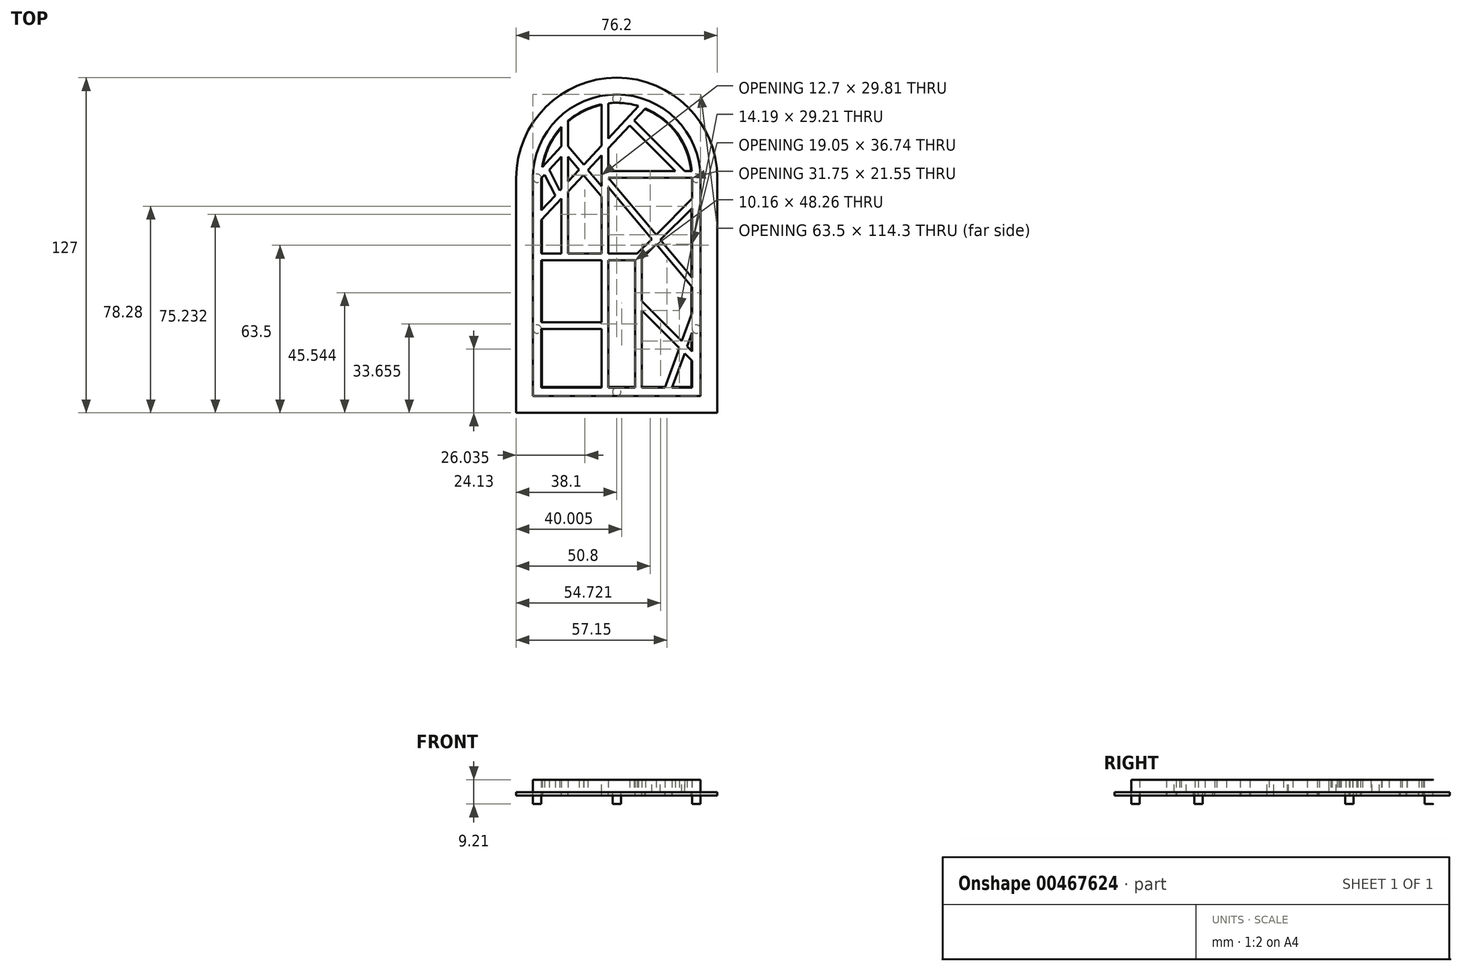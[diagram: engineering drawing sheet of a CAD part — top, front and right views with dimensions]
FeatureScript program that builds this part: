
annotation { "Feature Type Name" : "Feature", "Feature Type Description" : "" }
export const myFeature = defineFeature(function(context is Context, id is Id, definition is map)
    precondition{}
    {
        {
            var Q0;
            Q0=qCreatedBy(makeId("Top.planeOp"),FACE);
            var sketch = newSketch(context, id + "F0", { "sketchPlane" : qUnion([Q0])});
            skArc(sketch, "E0", {"start": v(31.75, 82.55) * mm, "mid": v(0, 114.3) * mm, "end": v(-31.75, 82.55) * mm});
            skLineSegment(sketch, "E1", {"start": v(31.75, 82.55) * mm, "end": v(31.75, 0) * mm});
            skLineSegment(sketch, "E2", {"start": v(31.75, 0) * mm, "end": v(-31.75, 0) * mm});
            skLineSegment(sketch, "E3", {"start": v(-31.75, 0) * mm, "end": v(-31.75, 82.55) * mm});
            skLineSegment(sketch, "E4.0", {"start": v(-28.58, 3.17) * mm, "end": v(-28.58, 82.55) * mm});
            skLineSegment(sketch, "E4.1", {"start": v(28.58, 3.18) * mm, "end": v(-28.58, 3.17) * mm});
            skLineSegment(sketch, "E4.2", {"start": v(28.57, 82.55) * mm, "end": v(28.58, 3.17) * mm});
            skArc(sketch, "E4.3", {"start": v(28.57, 82.55) * mm, "mid": v(0, 111.13) * mm, "end": v(-28.57, 82.55) * mm});
            skSolve(sketch);
        }
        {
            var Q0;
            Q0 = qSketchRegion(id + "F0", true);
            extrude(context, id + "F1", {"entities" : qUnion([Q0]), "depth" : 4.76 * mm});
        }
        {
            var Q0;
            Q0=qCreatedBy(makeId("Top.planeOp"),FACE);
            var sketch = newSketch(context, id + "F2", { "sketchPlane" : qUnion([Q0])});
            skLineSegment(sketch, "E5", {"start": v(-28.58, 53.98) * mm, "end": v(9.52, 53.98) * mm});
            skLineSegment(sketch, "E6", {"start": v(9.52, 53.98) * mm, "end": v(9.52, 3.17) * mm});
            skLineSegment(sketch, "E7", {"start": v(9.52, 3.17) * mm, "end": v(9.52, 3.17) * mm});
            skLineSegment(sketch, "E8", {"start": v(-28.58, 53.98) * mm, "end": v(-28.58, 51.43) * mm});
            skLineSegment(sketch, "E9", {"start": v(-28.58, 51.43) * mm, "end": v(6.98, 51.43) * mm});
            skLineSegment(sketch, "E10", {"start": v(6.98, 51.43) * mm, "end": v(6.98, 3.17) * mm});
            skLineSegment(sketch, "E11", {"start": v(6.98, 3.17) * mm, "end": v(9.52, 3.17) * mm});
            skSolve(sketch);
        }
        {
            var Q0;
            Q0 = qSketchRegion(id + "F2", true);
            var sketch = newSketch(context, id + "F3", { "sketchPlane" : qUnion([Q0])});
            skSolve(sketch);
        }
        {
            var Q0;
            Q0=makeQuery(id+"F3.imprint","IMPRINT",FACE,{"disambiguationData":[TD([[makeQuery(id+"F3.imprint","IMPRINT",EDGE,{"derivedFrom":makeQuery(id+"F2.imprint","IMPRINT",EDGE,{"derivedFrom":sQuery(id+"F2.wireOp",EDGE,"E5")})}),-1.0]])]});
            extrude(context, id + "F4", {"entities" : qUnion([Q0]), "operationType" : NewBodyOperationType.ADD, "depth" : 4.76 * mm});
        }
        {
            var Q0;
            Q0=qCreatedBy(makeId("Top.planeOp"),FACE);
            var sketch = newSketch(context, id + "F5", { "sketchPlane" : qUnion([Q0])});
            skLineSegment(sketch, "E12.bottom", {"start": v(-5.72, 3.17) * mm, "end": v(-3.18, 3.17) * mm});
            skLineSegment(sketch, "E12.left", {"start": v(-5.72, 3.17) * mm, "end": v(-5.72, 110.55) * mm});
            skLineSegment(sketch, "E12.right", {"start": v(-3.18, 3.17) * mm, "end": v(-3.18, 110.95) * mm});
            skArc(sketch, "E13.0", {"start": v(-3.18, 110.95) * mm, "mid": v(-4.45, 110.78) * mm, "end": v(-5.72, 110.55) * mm});
            skPoint(sketch, "E14.orphan", {"position": v(28.57, 82.55) * mm});
            skPoint(sketch, "E15.orphan", {"position": v(-28.57, 82.55) * mm});
            skSolve(sketch);
        }
        {
            var Q0;
            Q0 = qSketchRegion(id + "F5", true);
            extrude(context, id + "F6", {"entities" : qUnion([Q0]), "operationType" : NewBodyOperationType.ADD, "depth" : 4.76 * mm});
        }
        {
            var Q0;
            Q0=qCreatedBy(makeId("Top.planeOp"),FACE);
            var sketch = newSketch(context, id + "F7", { "sketchPlane" : qUnion([Q0])});
            skLineSegment(sketch, "E16.bottom", {"start": v(-28.58, 27.94) * mm, "end": v(-5.72, 27.94) * mm});
            skLineSegment(sketch, "E16.top", {"start": v(-28.58, 25.4) * mm, "end": v(-5.72, 25.4) * mm});
            skLineSegment(sketch, "E16.left", {"start": v(-28.58, 27.94) * mm, "end": v(-28.58, 25.4) * mm});
            skLineSegment(sketch, "E16.right", {"start": v(-5.72, 27.94) * mm, "end": v(-5.72, 25.4) * mm});
            skSolve(sketch);
        }
        {
            var Q0;
            Q0 = qSketchRegion(id + "F7", true);
            extrude(context, id + "F8", {"entities" : qUnion([Q0]), "operationType" : NewBodyOperationType.ADD, "depth" : 4.76 * mm});
        }
        {
            var Q0;
            Q0=qCreatedBy(makeId("Top.planeOp"),FACE);
            var sketch = newSketch(context, id + "F9", { "sketchPlane" : qUnion([Q0])});
            skLineSegment(sketch, "E17", {"start": v(9.52, 35.98) * mm, "end": v(28.58, 16.93) * mm});
            skLineSegment(sketch, "E18", {"start": v(28.58, 16.93) * mm, "end": v(28.58, 13.34) * mm});
            skLineSegment(sketch, "E19", {"start": v(28.58, 13.33) * mm, "end": v(9.52, 32.38) * mm});
            skLineSegment(sketch, "E20", {"start": v(9.52, 32.38) * mm, "end": v(9.52, 35.98) * mm});
            skLineSegment(sketch, "E21", {"start": v(-3.17, 82.7) * mm, "end": v(28.58, 44.87) * mm});
            skLineSegment(sketch, "E22", {"start": v(28.58, 44.87) * mm, "end": v(28.58, 41.28) * mm});
            skLineSegment(sketch, "E23", {"start": v(28.58, 41.27) * mm, "end": v(-3.18, 79.11) * mm});
            skLineSegment(sketch, "E24", {"start": v(-3.18, 79.11) * mm, "end": v(-3.18, 82.7) * mm});
            skSolve(sketch);
        }
        {
            var Q0;
            Q0 = qSketchRegion(id + "F9", true);
            extrude(context, id + "F10", {"entities" : qUnion([Q0]), "operationType" : NewBodyOperationType.ADD, "depth" : 4.76 * mm});
        }
        {
            var Q0;
            Q0=qCreatedBy(makeId("Top.planeOp"),FACE);
            var sketch = newSketch(context, id + "F11", { "sketchPlane" : qUnion([Q0])});
            skLineSegment(sketch, "E25.bottom", {"start": v(-20.96, 53.98) * mm, "end": v(-18.42, 53.98) * mm});
            skLineSegment(sketch, "E25.left", {"start": v(-20.96, 53.98) * mm, "end": v(-20.96, 101.98) * mm});
            skLineSegment(sketch, "E25.right", {"start": v(-18.42, 53.98) * mm, "end": v(-18.42, 104.4) * mm});
            skArc(sketch, "E26.0", {"start": v(-18.42, 104.4) * mm, "mid": v(-19.72, 103.23) * mm, "end": v(-20.96, 101.98) * mm});
            skPoint(sketch, "E27.orphan", {"position": v(-5.72, 110.55) * mm});
            skPoint(sketch, "E28.orphan", {"position": v(-28.57, 82.55) * mm});
            skSolve(sketch);
        }
        {
            var Q0;
            Q0 = qSketchRegion(id + "F11", true);
            extrude(context, id + "F12", {"entities" : qUnion([Q0]), "operationType" : NewBodyOperationType.ADD, "depth" : 4.76 * mm});
        }
        {
            var Q0;
            Q0=qCreatedBy(makeId("Top.planeOp"),FACE);
            var sketch = newSketch(context, id + "F13", { "sketchPlane" : qUnion([Q0])});
            skLineSegment(sketch, "E29", {"start": v(-28.58, 70.4) * mm, "end": v(8.26, 109.9) * mm});
            skLineSegment(sketch, "E30", {"start": v(10.87, 108.98) * mm, "end": v(-28.58, 66.67) * mm});
            skLineSegment(sketch, "E31", {"start": v(-28.58, 66.67) * mm, "end": v(-28.58, 70.4) * mm});
            skArc(sketch, "E32.0", {"start": v(10.87, 108.98) * mm, "mid": v(9.58, 109.47) * mm, "end": v(8.26, 109.9) * mm});
            skPoint(sketch, "E33.orphan", {"position": v(28.57, 82.55) * mm});
            skPoint(sketch, "E34.orphan", {"position": v(-3.18, 110.95) * mm});
            skLineSegment(sketch, "E35", {"start": v(7.73, 53.98) * mm, "end": v(9.52, 52.18) * mm});
            skLineSegment(sketch, "E36", {"start": v(9.52, 52.18) * mm, "end": v(28.58, 71.23) * mm});
            skLineSegment(sketch, "E37", {"start": v(28.58, 71.23) * mm, "end": v(28.58, 74.82) * mm});
            skLineSegment(sketch, "E38", {"start": v(28.58, 74.82) * mm, "end": v(7.73, 53.98) * mm});
            skLineSegment(sketch, "E39", {"start": v(18.25, 3.17) * mm, "end": v(28.58, 31.54) * mm});
            skLineSegment(sketch, "E40", {"start": v(28.58, 31.54) * mm, "end": v(28.58, 24.11) * mm});
            skLineSegment(sketch, "E41", {"start": v(28.58, 24.11) * mm, "end": v(20.96, 3.17) * mm});
            skLineSegment(sketch, "E42", {"start": v(20.96, 3.17) * mm, "end": v(18.25, 3.17) * mm});
            skSolve(sketch);
        }
        {
            var Q0;
            Q0 = qSketchRegion(id + "F13", true);
            extrude(context, id + "F14", {"entities" : qUnion([Q0]), "operationType" : NewBodyOperationType.ADD, "depth" : 4.76 * mm});
        }
        {
            var Q0;
            Q0=qCreatedBy(makeId("Top.planeOp"),FACE);
            var sketch = newSketch(context, id + "F15", { "sketchPlane" : qUnion([Q0])});
            skLineSegment(sketch, "E43", {"start": v(-18.42, 94.65) * mm, "end": v(-12.52, 87.62) * mm});
            skLineSegment(sketch, "E44", {"start": v(-5.72, 79.52) * mm, "end": v(-5.72, 75.57) * mm});
            skLineSegment(sketch, "E45", {"start": v(-5.72, 75.57) * mm, "end": v(-12.62, 83.79) * mm});
            skLineSegment(sketch, "E46", {"start": v(-18.42, 90.7) * mm, "end": v(-18.42, 94.65) * mm});
            skLineSegment(sketch, "E47", {"start": v(-20.96, 94.65) * mm, "end": v(-28.25, 86.83) * mm});
            skLineSegment(sketch, "E48", {"start": v(-28.58, 82.55) * mm, "end": v(-20.96, 90.72) * mm});
            skLineSegment(sketch, "E49", {"start": v(-20.96, 94.65) * mm, "end": v(-20.96, 90.72) * mm});
            skLineSegment(sketch, "E50.bottom", {"start": v(-3.18, 85.25) * mm, "end": v(28.45, 85.25) * mm});
            skLineSegment(sketch, "E50.top", {"start": v(-3.17, 82.7) * mm, "end": v(28.57, 82.7) * mm});
            skLineSegment(sketch, "E50.left", {"start": v(-3.18, 85.25) * mm, "end": v(-3.18, 82.7) * mm});
            skPoint(sketch, "E51.orphan", {"position": v(10.87, 108.98) * mm});
            skPoint(sketch, "E52.orphan", {"position": v(28.57, 82.55) * mm});
            skLineSegment(sketch, "E53.0", {"start": v(-10.87, 85.66) * mm, "end": v(-12.62, 83.79) * mm});
            skLineSegment(sketch, "E53.1", {"start": v(-14.26, 85.75) * mm, "end": v(-12.52, 87.62) * mm});
            skLineSegment(sketch, "E54.trimOffspring", {"start": v(-10.87, 85.66) * mm, "end": v(-5.72, 79.52) * mm});
            skLineSegment(sketch, "E55.trimOffspring", {"start": v(-14.26, 85.75) * mm, "end": v(-18.42, 90.7) * mm});
            skArc(sketch, "E56.0", {"start": v(-28.25, 86.83) * mm, "mid": v(-28.5, 84.7) * mm, "end": v(-28.58, 82.55) * mm});
            skPoint(sketch, "E57.orphan", {"position": v(-28.57, 82.55) * mm});
            skArc(sketch, "E58.0", {"start": v(28.57, 82.7) * mm, "mid": v(28.54, 83.98) * mm, "end": v(28.45, 85.25) * mm});
            skSolve(sketch);
        }
        {
            var Q0;
            Q0 = qSketchRegion(id + "F15", true);
            extrude(context, id + "F16", {"entities" : qUnion([Q0]), "operationType" : NewBodyOperationType.ADD, "depth" : 4.76 * mm});
        }
        {
            var Q0;
            Q0=qCreatedBy(makeId("Top.planeOp"),FACE);
            var sketch = newSketch(context, id + "F17", { "sketchPlane" : qUnion([Q0])});
            skLineSegment(sketch, "E59", {"start": v(4.9, 102.57) * mm, "end": v(22.23, 85.25) * mm});
            skLineSegment(sketch, "E60", {"start": v(22.22, 85.25) * mm, "end": v(25.82, 85.25) * mm});
            skLineSegment(sketch, "E61", {"start": v(25.82, 85.25) * mm, "end": v(6.63, 104.43) * mm});
            skLineSegment(sketch, "E62", {"start": v(6.63, 104.43) * mm, "end": v(4.9, 102.57) * mm});
            skLineSegment(sketch, "E63", {"start": v(-27.33, 83.89) * mm, "end": v(-23.32, 76.03) * mm});
            skLineSegment(sketch, "E64", {"start": v(-23.32, 76.03) * mm, "end": v(-21.6, 77.89) * mm});
            skLineSegment(sketch, "E65", {"start": v(-21.6, 77.89) * mm, "end": v(-25.6, 85.75) * mm});
            skLineSegment(sketch, "E66", {"start": v(-25.6, 85.75) * mm, "end": v(-27.33, 83.89) * mm});
            skSolve(sketch);
        }
        {
            var Q0;
            Q0 = qSketchRegion(id + "F17", true);
            extrude(context, id + "F18", {"entities" : qUnion([Q0]), "operationType" : NewBodyOperationType.ADD, "depth" : 4.76 * mm});
        }
        {
            var Q0;
            Q0=makeQuery(id+"F18.boolean.opBoolean","MERGE",FACE,{"derivedFrom":[makeQuery(id+"F16.boolean.opBoolean","MERGE",FACE,{"derivedFrom":[makeQuery(id+"F14.boolean.opBoolean","MERGE",FACE,{"derivedFrom":[makeQuery(id+"F12.boolean.opBoolean","MERGE",FACE,{"derivedFrom":[makeQuery(id+"F10.boolean.opBoolean","MERGE",FACE,{"derivedFrom":[makeQuery(id+"F8.boolean.opBoolean","MERGE",FACE,{"derivedFrom":[makeQuery(id+"F6.boolean.opBoolean","MERGE",FACE,{"derivedFrom":[makeQuery(id+"F4.boolean.opBoolean","MERGE",FACE,{"derivedFrom":[makeQuery(id+"F1.opExtrude","CAP_FACE",FACE,{"disambiguationData":[OSD([sQuery(id+"F0.wireOp",EDGE,"E0"),sQuery(id+"F0.wireOp",EDGE,"E1"),sQuery(id+"F0.wireOp",EDGE,"E2"),sQuery(id+"F0.wireOp",EDGE,"E3"),sQuery(id+"F0.wireOp",EDGE,"E4.0"),sQuery(id+"F0.wireOp",EDGE,"E4.1"),sQuery(id+"F0.wireOp",EDGE,"E4.2"),sQuery(id+"F0.wireOp",EDGE,"E4.3")])],"isStart":true}),makeQuery(id+"F4.opExtrude","CAP_FACE",FACE,{"disambiguationData":[OSD([sQuery(id+"F2.wireOp",EDGE,"E5"),sQuery(id+"F2.wireOp",EDGE,"E6"),sQuery(id+"F2.wireOp",EDGE,"E8"),sQuery(id+"F2.wireOp",EDGE,"E9"),sQuery(id+"F2.wireOp",EDGE,"E10"),sQuery(id+"F2.wireOp",EDGE,"E11")])],"isStart":true})]}),makeQuery(id+"F6.opExtrude","CAP_FACE",FACE,{"disambiguationData":[OSD([sQuery(id+"F5.wireOp",EDGE,"E12.bottom"),sQuery(id+"F5.wireOp",EDGE,"E12.left"),sQuery(id+"F5.wireOp",EDGE,"E12.right"),sQuery(id+"F5.wireOp",EDGE,"E13.0")])],"isStart":true})]}),makeQuery(id+"F8.opExtrude","CAP_FACE",FACE,{"disambiguationData":[OSD([sQuery(id+"F7.wireOp",EDGE,"E16.bottom"),sQuery(id+"F7.wireOp",EDGE,"E16.top"),sQuery(id+"F7.wireOp",EDGE,"E16.left"),sQuery(id+"F7.wireOp",EDGE,"E16.right")])],"isStart":true})]}),makeQuery(id+"F10.opExtrude","CAP_FACE",FACE,{"disambiguationData":[OSD([sQuery(id+"F9.wireOp",EDGE,"E17"),sQuery(id+"F9.wireOp",EDGE,"E18"),sQuery(id+"F9.wireOp",EDGE,"E19"),sQuery(id+"F9.wireOp",EDGE,"E20")])],"isStart":true}),makeQuery(id+"F10.opExtrude","CAP_FACE",FACE,{"disambiguationData":[OSD([sQuery(id+"F9.wireOp",EDGE,"E21"),sQuery(id+"F9.wireOp",EDGE,"E22"),sQuery(id+"F9.wireOp",EDGE,"E23"),sQuery(id+"F9.wireOp",EDGE,"E24")])],"isStart":true})]}),makeQuery(id+"F12.opExtrude","CAP_FACE",FACE,{"disambiguationData":[OSD([sQuery(id+"F11.wireOp",EDGE,"E25.bottom"),sQuery(id+"F11.wireOp",EDGE,"E25.left"),sQuery(id+"F11.wireOp",EDGE,"E25.right"),sQuery(id+"F11.wireOp",EDGE,"E26.0")])],"isStart":true})]}),makeQuery(id+"F14.opExtrude","CAP_FACE",FACE,{"disambiguationData":[OSD([sQuery(id+"F13.wireOp",EDGE,"E29"),sQuery(id+"F13.wireOp",EDGE,"E30"),sQuery(id+"F13.wireOp",EDGE,"E31"),sQuery(id+"F13.wireOp",EDGE,"E32.0")])],"isStart":true}),makeQuery(id+"F14.opExtrude","CAP_FACE",FACE,{"disambiguationData":[OSD([sQuery(id+"F13.wireOp",EDGE,"E35"),sQuery(id+"F13.wireOp",EDGE,"E36"),sQuery(id+"F13.wireOp",EDGE,"E37"),sQuery(id+"F13.wireOp",EDGE,"E38")])],"isStart":true}),makeQuery(id+"F14.opExtrude","CAP_FACE",FACE,{"disambiguationData":[OSD([sQuery(id+"F13.wireOp",EDGE,"E39"),sQuery(id+"F13.wireOp",EDGE,"E40"),sQuery(id+"F13.wireOp",EDGE,"E41"),sQuery(id+"F13.wireOp",EDGE,"E42")])],"isStart":true})]}),makeQuery(id+"F16.opExtrude","CAP_FACE",FACE,{"disambiguationData":[OSD([sQuery(id+"F15.wireOp",EDGE,"E43"),sQuery(id+"F15.wireOp",EDGE,"E46"),sQuery(id+"F15.wireOp",EDGE,"E53.1"),sQuery(id+"F15.wireOp",EDGE,"E55.trimOffspring")])],"isStart":true}),makeQuery(id+"F16.opExtrude","CAP_FACE",FACE,{"disambiguationData":[OSD([sQuery(id+"F15.wireOp",EDGE,"E44"),sQuery(id+"F15.wireOp",EDGE,"E45"),sQuery(id+"F15.wireOp",EDGE,"E53.0"),sQuery(id+"F15.wireOp",EDGE,"E54.trimOffspring")])],"isStart":true}),makeQuery(id+"F16.opExtrude","CAP_FACE",FACE,{"disambiguationData":[OSD([sQuery(id+"F15.wireOp",EDGE,"E47"),sQuery(id+"F15.wireOp",EDGE,"E48"),sQuery(id+"F15.wireOp",EDGE,"E49"),sQuery(id+"F15.wireOp",EDGE,"E56.0")])],"isStart":true}),makeQuery(id+"F16.opExtrude","CAP_FACE",FACE,{"disambiguationData":[OSD([sQuery(id+"F15.wireOp",EDGE,"E50.bottom"),sQuery(id+"F15.wireOp",EDGE,"E50.top"),sQuery(id+"F15.wireOp",EDGE,"E50.left"),sQuery(id+"F15.wireOp",EDGE,"E58.0")])],"isStart":true})]}),makeQuery(id+"F18.opExtrude","CAP_FACE",FACE,{"disambiguationData":[OSD([sQuery(id+"F17.wireOp",EDGE,"E59"),sQuery(id+"F17.wireOp",EDGE,"E60"),sQuery(id+"F17.wireOp",EDGE,"E61"),sQuery(id+"F17.wireOp",EDGE,"E62")])],"isStart":true}),makeQuery(id+"F18.opExtrude","CAP_FACE",FACE,{"disambiguationData":[OSD([sQuery(id+"F17.wireOp",EDGE,"E63"),sQuery(id+"F17.wireOp",EDGE,"E64"),sQuery(id+"F17.wireOp",EDGE,"E65"),sQuery(id+"F17.wireOp",EDGE,"E66")])],"isStart":true})]});
            var sketch = newSketch(context, id + "F19", { "sketchPlane" : qUnion([Q0])});
            skCircle(sketch, "E67", {"center": v(0, -112.71) * mm, "radius": 1.59 * mm});
            skLineSegment(sketch, "E68", {"start": v(0, -114.3) * mm, "end": v(0, -111.13) * mm, "construction": true});
            skLineSegment(sketch, "E69", {"start": v(28.57, -82.55) * mm, "end": v(31.75, -82.55) * mm, "construction": true});
            skLineSegment(sketch, "E70", {"start": v(-28.58, -82.55) * mm, "end": v(-31.75, -82.55) * mm, "construction": true});
            skLineSegment(sketch, "E71", {"start": v(0, 0) * mm, "end": v(0, -3.17) * mm, "construction": true});
            skLineSegment(sketch, "E72", {"start": v(31.75, -25.4) * mm, "end": v(28.58, -25.4) * mm, "construction": true});
            skLineSegment(sketch, "E73", {"start": v(-31.75, -25.4) * mm, "end": v(-28.58, -25.4) * mm, "construction": true});
            skLineSegment(sketch, "E74", {"start": v(28.58, -25.4) * mm, "end": v(-28.58, -25.4) * mm, "construction": true});
            skCircle(sketch, "E75", {"center": v(-30.16, -25.4) * mm, "radius": 1.59 * mm});
            skCircle(sketch, "E76", {"center": v(30.16, -25.4) * mm, "radius": 1.59 * mm});
            skCircle(sketch, "E77", {"center": v(0, -1.59) * mm, "radius": 1.59 * mm});
            skCircle(sketch, "E78", {"center": v(-30.16, -82.55) * mm, "radius": 1.59 * mm});
            skCircle(sketch, "E79", {"center": v(30.16, -82.55) * mm, "radius": 1.59 * mm});
            skSolve(sketch);
        }
        {
            var Q0;
            Q0 = qSketchRegion(id + "F19", true);
            extrude(context, id + "F20", {"entities" : qUnion([Q0]), "operationType" : NewBodyOperationType.ADD, "depth" : 4.44 * mm});
        }
        {
            var Q0;
            Q0=makeQuery(id+"F18.boolean.opBoolean","MERGE",FACE,{"derivedFrom":[makeQuery(id+"F16.boolean.opBoolean","MERGE",FACE,{"derivedFrom":[makeQuery(id+"F14.boolean.opBoolean","MERGE",FACE,{"derivedFrom":[makeQuery(id+"F12.boolean.opBoolean","MERGE",FACE,{"derivedFrom":[makeQuery(id+"F10.boolean.opBoolean","MERGE",FACE,{"derivedFrom":[makeQuery(id+"F8.boolean.opBoolean","MERGE",FACE,{"derivedFrom":[makeQuery(id+"F6.boolean.opBoolean","MERGE",FACE,{"derivedFrom":[makeQuery(id+"F4.boolean.opBoolean","MERGE",FACE,{"derivedFrom":[makeQuery(id+"F1.opExtrude","CAP_FACE",FACE,{"disambiguationData":[OSD([sQuery(id+"F0.wireOp",EDGE,"E0"),sQuery(id+"F0.wireOp",EDGE,"E1"),sQuery(id+"F0.wireOp",EDGE,"E2"),sQuery(id+"F0.wireOp",EDGE,"E3"),sQuery(id+"F0.wireOp",EDGE,"E4.0"),sQuery(id+"F0.wireOp",EDGE,"E4.1"),sQuery(id+"F0.wireOp",EDGE,"E4.2"),sQuery(id+"F0.wireOp",EDGE,"E4.3")])],"isStart":true}),makeQuery(id+"F4.opExtrude","CAP_FACE",FACE,{"disambiguationData":[OSD([sQuery(id+"F2.wireOp",EDGE,"E5"),sQuery(id+"F2.wireOp",EDGE,"E6"),sQuery(id+"F2.wireOp",EDGE,"E8"),sQuery(id+"F2.wireOp",EDGE,"E9"),sQuery(id+"F2.wireOp",EDGE,"E10"),sQuery(id+"F2.wireOp",EDGE,"E11")])],"isStart":true})]}),makeQuery(id+"F6.opExtrude","CAP_FACE",FACE,{"disambiguationData":[OSD([sQuery(id+"F5.wireOp",EDGE,"E12.bottom"),sQuery(id+"F5.wireOp",EDGE,"E12.left"),sQuery(id+"F5.wireOp",EDGE,"E12.right"),sQuery(id+"F5.wireOp",EDGE,"E13.0")])],"isStart":true})]}),makeQuery(id+"F8.opExtrude","CAP_FACE",FACE,{"disambiguationData":[OSD([sQuery(id+"F7.wireOp",EDGE,"E16.bottom"),sQuery(id+"F7.wireOp",EDGE,"E16.top"),sQuery(id+"F7.wireOp",EDGE,"E16.left"),sQuery(id+"F7.wireOp",EDGE,"E16.right")])],"isStart":true})]}),makeQuery(id+"F10.opExtrude","CAP_FACE",FACE,{"disambiguationData":[OSD([sQuery(id+"F9.wireOp",EDGE,"E17"),sQuery(id+"F9.wireOp",EDGE,"E18"),sQuery(id+"F9.wireOp",EDGE,"E19"),sQuery(id+"F9.wireOp",EDGE,"E20")])],"isStart":true}),makeQuery(id+"F10.opExtrude","CAP_FACE",FACE,{"disambiguationData":[OSD([sQuery(id+"F9.wireOp",EDGE,"E21"),sQuery(id+"F9.wireOp",EDGE,"E22"),sQuery(id+"F9.wireOp",EDGE,"E23"),sQuery(id+"F9.wireOp",EDGE,"E24")])],"isStart":true})]}),makeQuery(id+"F12.opExtrude","CAP_FACE",FACE,{"disambiguationData":[OSD([sQuery(id+"F11.wireOp",EDGE,"E25.bottom"),sQuery(id+"F11.wireOp",EDGE,"E25.left"),sQuery(id+"F11.wireOp",EDGE,"E25.right"),sQuery(id+"F11.wireOp",EDGE,"E26.0")])],"isStart":true})]}),makeQuery(id+"F14.opExtrude","CAP_FACE",FACE,{"disambiguationData":[OSD([sQuery(id+"F13.wireOp",EDGE,"E29"),sQuery(id+"F13.wireOp",EDGE,"E30"),sQuery(id+"F13.wireOp",EDGE,"E31"),sQuery(id+"F13.wireOp",EDGE,"E32.0")])],"isStart":true}),makeQuery(id+"F14.opExtrude","CAP_FACE",FACE,{"disambiguationData":[OSD([sQuery(id+"F13.wireOp",EDGE,"E35"),sQuery(id+"F13.wireOp",EDGE,"E36"),sQuery(id+"F13.wireOp",EDGE,"E37"),sQuery(id+"F13.wireOp",EDGE,"E38")])],"isStart":true}),makeQuery(id+"F14.opExtrude","CAP_FACE",FACE,{"disambiguationData":[OSD([sQuery(id+"F13.wireOp",EDGE,"E39"),sQuery(id+"F13.wireOp",EDGE,"E40"),sQuery(id+"F13.wireOp",EDGE,"E41"),sQuery(id+"F13.wireOp",EDGE,"E42")])],"isStart":true})]}),makeQuery(id+"F16.opExtrude","CAP_FACE",FACE,{"disambiguationData":[OSD([sQuery(id+"F15.wireOp",EDGE,"E43"),sQuery(id+"F15.wireOp",EDGE,"E46"),sQuery(id+"F15.wireOp",EDGE,"E53.1"),sQuery(id+"F15.wireOp",EDGE,"E55.trimOffspring")])],"isStart":true}),makeQuery(id+"F16.opExtrude","CAP_FACE",FACE,{"disambiguationData":[OSD([sQuery(id+"F15.wireOp",EDGE,"E44"),sQuery(id+"F15.wireOp",EDGE,"E45"),sQuery(id+"F15.wireOp",EDGE,"E53.0"),sQuery(id+"F15.wireOp",EDGE,"E54.trimOffspring")])],"isStart":true}),makeQuery(id+"F16.opExtrude","CAP_FACE",FACE,{"disambiguationData":[OSD([sQuery(id+"F15.wireOp",EDGE,"E47"),sQuery(id+"F15.wireOp",EDGE,"E48"),sQuery(id+"F15.wireOp",EDGE,"E49"),sQuery(id+"F15.wireOp",EDGE,"E56.0")])],"isStart":true}),makeQuery(id+"F16.opExtrude","CAP_FACE",FACE,{"disambiguationData":[OSD([sQuery(id+"F15.wireOp",EDGE,"E50.bottom"),sQuery(id+"F15.wireOp",EDGE,"E50.top"),sQuery(id+"F15.wireOp",EDGE,"E50.left"),sQuery(id+"F15.wireOp",EDGE,"E58.0")])],"isStart":true})]}),makeQuery(id+"F18.opExtrude","CAP_FACE",FACE,{"disambiguationData":[OSD([sQuery(id+"F17.wireOp",EDGE,"E59"),sQuery(id+"F17.wireOp",EDGE,"E60"),sQuery(id+"F17.wireOp",EDGE,"E61"),sQuery(id+"F17.wireOp",EDGE,"E62")])],"isStart":true}),makeQuery(id+"F18.opExtrude","CAP_FACE",FACE,{"disambiguationData":[OSD([sQuery(id+"F17.wireOp",EDGE,"E63"),sQuery(id+"F17.wireOp",EDGE,"E64"),sQuery(id+"F17.wireOp",EDGE,"E65"),sQuery(id+"F17.wireOp",EDGE,"E66")])],"isStart":true})]});
            var sketch = newSketch(context, id + "F21", { "sketchPlane" : qUnion([Q0])});
            skLineSegment(sketch, "E80.0", {"start": v(-31.75, -25.4) * mm, "end": v(-31.75, -82.55) * mm, "construction": true});
            skArc(sketch, "E80.1", {"start": v(0, -114.3) * mm, "mid": v(-22.45, -105) * mm, "end": v(-31.75, -82.55) * mm, "construction": true});
            skArc(sketch, "E80.2", {"start": v(31.75, -82.55) * mm, "mid": v(22.45, -105) * mm, "end": v(0, -114.3) * mm, "construction": true});
            skLineSegment(sketch, "E80.3", {"start": v(31.75, -82.55) * mm, "end": v(31.75, -25.4) * mm, "construction": true});
            skLineSegment(sketch, "E80.4", {"start": v(31.75, -25.4) * mm, "end": v(31.75, 0) * mm, "construction": true});
            skLineSegment(sketch, "E80.5", {"start": v(31.75, 0) * mm, "end": v(0, 0) * mm, "construction": true});
            skLineSegment(sketch, "E80.6", {"start": v(0, 0) * mm, "end": v(-31.75, 0) * mm, "construction": true});
            skLineSegment(sketch, "E80.7", {"start": v(-31.75, 0) * mm, "end": v(-31.75, -25.4) * mm, "construction": true});
            skLineSegment(sketch, "E81.0", {"start": v(28.32, -82.55) * mm, "end": v(28.32, -25.4) * mm});
            skLineSegment(sketch, "E81.1", {"start": v(28.32, -25.4) * mm, "end": v(28.32, -3.43) * mm});
            skArc(sketch, "E81.2", {"start": v(28.32, -82.55) * mm, "mid": v(20.03, -102.58) * mm, "end": v(0, -110.87) * mm});
            skLineSegment(sketch, "E81.3", {"start": v(28.32, -3.43) * mm, "end": v(0, -3.43) * mm});
            skArc(sketch, "E81.4", {"start": v(0, -110.87) * mm, "mid": v(-20.03, -102.58) * mm, "end": v(-28.32, -82.55) * mm});
            skLineSegment(sketch, "E81.5", {"start": v(-28.32, -25.4) * mm, "end": v(-28.32, -82.55) * mm});
            skLineSegment(sketch, "E81.6", {"start": v(-28.32, -3.43) * mm, "end": v(-28.32, -25.4) * mm});
            skLineSegment(sketch, "E81.7", {"start": v(0, -3.43) * mm, "end": v(-28.32, -3.43) * mm});
            skLineSegment(sketch, "E82.0", {"start": v(-38.1, 6.35) * mm, "end": v(-38.1, -25.4) * mm});
            skLineSegment(sketch, "E82.1", {"start": v(0, 6.35) * mm, "end": v(-38.1, 6.35) * mm});
            skLineSegment(sketch, "E82.2", {"start": v(-38.1, -25.4) * mm, "end": v(-38.1, -82.55) * mm});
            skLineSegment(sketch, "E82.3", {"start": v(38.1, 6.35) * mm, "end": v(0, 6.35) * mm});
            skArc(sketch, "E82.4", {"start": v(0, -120.65) * mm, "mid": v(-26.94, -109.5) * mm, "end": v(-38.1, -82.55) * mm});
            skArc(sketch, "E82.5", {"start": v(38.1, -82.55) * mm, "mid": v(26.94, -109.5) * mm, "end": v(0, -120.65) * mm});
            skLineSegment(sketch, "E82.6", {"start": v(38.1, -82.55) * mm, "end": v(38.1, -25.4) * mm});
            skLineSegment(sketch, "E82.7", {"start": v(38.1, -25.4) * mm, "end": v(38.1, 6.35) * mm});
            skSolve(sketch);
        }
        {
            var Q0;
            {var subQ28=sQuery(id+"F19.wireOp",EDGE,"E67");Q0=makeQuery(id+"F21.imprint","IMPRINT",FACE,{"disambiguationData":[TD([[makeQuery(id+"F21.imprint","IMPRINT",EDGE,{"derivedFrom":makeQuery(id+"F20.boolean.opBoolean","SPLIT",EDGE,{"disambiguationData":[OD(0.0)],"derivedFrom":makeQuery(id+"F20.opExtrude","CAP_EDGE",EDGE,{"disambiguationData":[OSD([subQ28])],"isStart":true})})}),-1.0]])]});}
            var Q1;
            {var subQ39=sQuery(id+"F19.wireOp",EDGE,"E76");Q1=makeQuery(id+"F21.imprint","IMPRINT",FACE,{"disambiguationData":[TD([[makeQuery(id+"F21.imprint","IMPRINT",EDGE,{"derivedFrom":makeQuery(id+"F20.opExtrude","CAP_EDGE",EDGE,{"disambiguationData":[OSD([subQ39])],"isStart":true})}),-1.0]])]});}
            var Q2;
            {var subQ21=sQuery(id+"F21.wireOp",EDGE,"E81.2");var subQ26=sQuery(id+"F21.wireOp",EDGE,"E81.0");var subQ27=makeQuery(id+"F21.imprint","INTERSECT",VERTEX,{"derivedFrom":[subQ26,subQ21]});Q2=makeQuery(id+"F21.imprint","IMPRINT",FACE,{"disambiguationData":[TD([[makeQuery(id+"F21.imprint","IMPRINT",EDGE,{"disambiguationData":[TD([[subQ27,-1.0]])],"derivedFrom":subQ21}),1.0]])]});}
            var Q3;
            Q3=makeQuery(id+"F21.imprint","IMPRINT",FACE,{"disambiguationData":[TD([[makeQuery(id+"F21.imprint","IMPRINT",EDGE,{"derivedFrom":sQuery(id+"F21.wireOp",EDGE,"E82.0")}),1.0]])]});
            var Q4;
            {var subQ1=sQuery(id+"F13.wireOp",EDGE,"E30");var subQ8=sQuery(id+"F0.wireOp",EDGE,"E4.3");var subQ9=sQuery(id+"F0.wireOp",EDGE,"E4.2");var subQ28=makeQuery(id+"F14.opExtrude","SWEPT_FACE",FACE,{"disambiguationData":[OSD([subQ1])]});var subQ32=makeQuery(id+"F1.opExtrude","SWEPT_FACE",FACE,{"disambiguationData":[OSD([subQ9])]});var subQ33=makeQuery(id+"F16.boolean.opBoolean","SPLIT",EDGE,{"disambiguationData":[TD([subQ28])],"derivedFrom":makeQuery(id+"F14.boolean.opBoolean","SPLIT",EDGE,{"disambiguationData":[TD([subQ32])],"derivedFrom":makeQuery(id+"F6.boolean.opBoolean","SPLIT",EDGE,{"disambiguationData":[TD([subQ32])],"derivedFrom":makeQuery(id+"F1.opExtrude","CAP_EDGE",EDGE,{"disambiguationData":[OSD([subQ8])],"isStart":true})})})});Q4=makeQuery(id+"F21.imprint","IMPRINT",FACE,{"disambiguationData":[TD([[makeQuery(id+"F21.imprint","IMPRINT",EDGE,{"derivedFrom":subQ33}),-1.0]])]});}
            var Q5;
            {var subQ28=sQuery(id+"F21.wireOp",EDGE,"E81.4");var subQ29=sQuery(id+"F21.wireOp",EDGE,"E81.2");var subQ30=makeQuery(id+"F21.imprint","INTERSECT",VERTEX,{"derivedFrom":[subQ29,subQ28]});Q5=makeQuery(id+"F21.imprint","IMPRINT",FACE,{"disambiguationData":[TD([[makeQuery(id+"F21.imprint","IMPRINT",EDGE,{"disambiguationData":[TD([[subQ30,1.0]])],"derivedFrom":subQ29}),1.0]])]});}
            var Q6;
            {var subQ3=sQuery(id+"F19.wireOp",EDGE,"E67");Q6=makeQuery(id+"F21.imprint","IMPRINT",FACE,{"disambiguationData":[TD([[makeQuery(id+"F21.imprint","IMPRINT",EDGE,{"derivedFrom":makeQuery(id+"F20.boolean.opBoolean","SPLIT",EDGE,{"disambiguationData":[OD(1.0)],"derivedFrom":makeQuery(id+"F20.opExtrude","CAP_EDGE",EDGE,{"disambiguationData":[OSD([subQ3])],"isStart":true})})}),-1.0]])]});}
            var Q7;
            {var subQ4=sQuery(id+"F5.wireOp",EDGE,"E12.left");var subQ5=makeQuery(id+"F6.opExtrude","SWEPT_FACE",FACE,{"disambiguationData":[OSD([subQ4])]});var subQ8=sQuery(id+"F0.wireOp",EDGE,"E4.3");var subQ9=sQuery(id+"F0.wireOp",EDGE,"E4.0");var subQ26=makeQuery(id+"F12.boolean.opBoolean","SPLIT",EDGE,{"disambiguationData":[TD([subQ5])],"derivedFrom":makeQuery(id+"F6.boolean.opBoolean","SPLIT",EDGE,{"disambiguationData":[TD([makeQuery(id+"F1.opExtrude","SWEPT_FACE",FACE,{"disambiguationData":[OSD([subQ9])]})])],"derivedFrom":makeQuery(id+"F1.opExtrude","CAP_EDGE",EDGE,{"disambiguationData":[OSD([subQ8])],"isStart":true})})});Q7=makeQuery(id+"F21.imprint","IMPRINT",FACE,{"disambiguationData":[TD([[makeQuery(id+"F21.imprint","IMPRINT",EDGE,{"derivedFrom":subQ26}),-1.0]])]});}
            var Q8;
            {var subQ0=sQuery(id+"F21.wireOp",EDGE,"E81.4");var subQ6=sQuery(id+"F15.wireOp",EDGE,"E47");var subQ21=makeQuery(id+"F16.opExtrude","CAP_EDGE",EDGE,{"disambiguationData":[OSD([subQ6])],"isStart":true});var subQ22=makeQuery(id+"F21.imprint","INTERSECT",VERTEX,{"derivedFrom":[subQ21,subQ0]});Q8=makeQuery(id+"F21.imprint","IMPRINT",FACE,{"disambiguationData":[TD([[makeQuery(id+"F21.imprint","IMPRINT",EDGE,{"disambiguationData":[TD([[subQ22,-1.0]])],"derivedFrom":subQ21}),1.0]])]});}
            var Q9;
            {var subQ7=sQuery(id+"F0.wireOp",EDGE,"E4.0");var subQ15=sQuery(id+"F0.wireOp",EDGE,"E4.3");var subQ31=makeQuery(id+"F1.opExtrude","SWEPT_FACE",FACE,{"disambiguationData":[OSD([subQ15])]});var subQ32=makeQuery(id+"F14.boolean.opBoolean","SPLIT",EDGE,{"disambiguationData":[TD([subQ31])],"derivedFrom":makeQuery(id+"F4.boolean.opBoolean","SPLIT",EDGE,{"disambiguationData":[TD([subQ31])],"derivedFrom":makeQuery(id+"F1.opExtrude","CAP_EDGE",EDGE,{"disambiguationData":[OSD([subQ7])],"isStart":true})})});Q9=makeQuery(id+"F21.imprint","IMPRINT",FACE,{"disambiguationData":[TD([[makeQuery(id+"F21.imprint","IMPRINT",EDGE,{"derivedFrom":subQ32}),1.0]])]});}
            var Q10;
            {var subQ32=sQuery(id+"F19.wireOp",EDGE,"E75");var subQ33=makeQuery(id+"F20.opExtrude","CAP_EDGE",EDGE,{"disambiguationData":[OSD([subQ32])],"isStart":true});var subQ34=makeQuery(id+"F20.boolean.opBoolean","SPLIT",EDGE,{"disambiguationData":[OD(1.0)],"derivedFrom":subQ33});Q10=makeQuery(id+"F21.imprint","IMPRINT",FACE,{"disambiguationData":[TD([[makeQuery(id+"F21.imprint","IMPRINT",EDGE,{"derivedFrom":subQ34}),-1.0]])]});}
            var Q11;
            {var subQ1=sQuery(id+"F2.wireOp",EDGE,"E5");var subQ2=makeQuery(id+"F4.opExtrude","SWEPT_FACE",FACE,{"disambiguationData":[OSD([subQ1])]});var subQ8=sQuery(id+"F0.wireOp",EDGE,"E4.0");var subQ10=sQuery(id+"F0.wireOp",EDGE,"E4.3");var subQ25=makeQuery(id+"F14.boolean.opBoolean","SPLIT",EDGE,{"disambiguationData":[TD([subQ2])],"derivedFrom":makeQuery(id+"F4.boolean.opBoolean","SPLIT",EDGE,{"disambiguationData":[TD([makeQuery(id+"F1.opExtrude","SWEPT_FACE",FACE,{"disambiguationData":[OSD([subQ10])]})])],"derivedFrom":makeQuery(id+"F1.opExtrude","CAP_EDGE",EDGE,{"disambiguationData":[OSD([subQ8])],"isStart":true})})});Q11=makeQuery(id+"F21.imprint","IMPRINT",FACE,{"disambiguationData":[TD([[makeQuery(id+"F21.imprint","IMPRINT",EDGE,{"derivedFrom":subQ25}),1.0]])]});}
            var Q12;
            {var subQ0=sQuery(id+"F21.wireOp",EDGE,"E81.5");var subQ1=sQuery(id+"F7.wireOp",EDGE,"E16.bottom");var subQ2=makeQuery(id+"F8.opExtrude","CAP_EDGE",EDGE,{"disambiguationData":[OSD([subQ1])],"isStart":true});var subQ3=makeQuery(id+"F21.imprint","INTERSECT",VERTEX,{"derivedFrom":[subQ2,subQ0]});Q12=makeQuery(id+"F21.imprint","IMPRINT",FACE,{"disambiguationData":[TD([[makeQuery(id+"F21.imprint","IMPRINT",EDGE,{"disambiguationData":[TD([[subQ3,-1.0]])],"derivedFrom":subQ0}),-1.0]])]});}
            var Q13;
            {var subQ44=sQuery(id+"F19.wireOp",EDGE,"E75");Q13=makeQuery(id+"F21.imprint","IMPRINT",FACE,{"disambiguationData":[TD([[makeQuery(id+"F21.imprint","IMPRINT",EDGE,{"derivedFrom":makeQuery(id+"F20.boolean.opBoolean","SPLIT",EDGE,{"disambiguationData":[OD(0.0)],"derivedFrom":makeQuery(id+"F20.opExtrude","CAP_EDGE",EDGE,{"disambiguationData":[OSD([subQ44])],"isStart":true})})}),-1.0]])]});}
            var Q14;
            {var subQ16=sQuery(id+"F21.wireOp",EDGE,"E81.6");Q14=makeQuery(id+"F21.imprint","IMPRINT",FACE,{"disambiguationData":[TD([[makeQuery(id+"F21.imprint","IMPRINT",EDGE,{"derivedFrom":subQ16}),-1.0]])]});}
            var Q15;
            {var subQ28=sQuery(id+"F21.wireOp",EDGE,"E81.7");var subQ29=sQuery(id+"F21.wireOp",EDGE,"E81.3");var subQ30=makeQuery(id+"F21.imprint","INTERSECT",VERTEX,{"derivedFrom":[subQ29,subQ28]});Q15=makeQuery(id+"F21.imprint","IMPRINT",FACE,{"disambiguationData":[TD([[makeQuery(id+"F21.imprint","IMPRINT",EDGE,{"disambiguationData":[TD([[subQ30,1.0]])],"derivedFrom":subQ29}),-1.0]])]});}
            var Q16;
            {var subQ8=sQuery(id+"F0.wireOp",EDGE,"E4.2");var subQ9=sQuery(id+"F0.wireOp",EDGE,"E4.1");var subQ11=sQuery(id+"F2.wireOp",EDGE,"E6");var subQ21=makeQuery(id+"F4.opExtrude","SWEPT_FACE",FACE,{"disambiguationData":[OSD([subQ11])]});var subQ24=makeQuery(id+"F14.boolean.opBoolean","SPLIT",EDGE,{"disambiguationData":[TD([subQ21])],"derivedFrom":makeQuery(id+"F4.boolean.opBoolean","SPLIT",EDGE,{"disambiguationData":[TD([makeQuery(id+"F1.opExtrude","SWEPT_FACE",FACE,{"disambiguationData":[OSD([subQ8])]})])],"derivedFrom":makeQuery(id+"F1.opExtrude","CAP_EDGE",EDGE,{"disambiguationData":[OSD([subQ9])],"isStart":true})})});Q16=makeQuery(id+"F21.imprint","IMPRINT",FACE,{"disambiguationData":[TD([[makeQuery(id+"F21.imprint","IMPRINT",EDGE,{"derivedFrom":subQ24}),1.0]])]});}
            var Q17;
            {var subQ6=sQuery(id+"F0.wireOp",EDGE,"E4.2");var subQ7=sQuery(id+"F0.wireOp",EDGE,"E4.1");var subQ11=makeQuery(id+"F1.opExtrude","SWEPT_FACE",FACE,{"disambiguationData":[OSD([subQ7])]});var subQ20=makeQuery(id+"F10.boolean.opBoolean","SPLIT",EDGE,{"disambiguationData":[TD([subQ11])],"derivedFrom":makeQuery(id+"F1.opExtrude","CAP_EDGE",EDGE,{"disambiguationData":[OSD([subQ6])],"isStart":true})});Q17=makeQuery(id+"F21.imprint","IMPRINT",FACE,{"disambiguationData":[TD([[makeQuery(id+"F21.imprint","IMPRINT",EDGE,{"derivedFrom":subQ20}),1.0]])]});}
            var Q18;
            {var subQ1=sQuery(id+"F9.wireOp",EDGE,"E17");var subQ4=makeQuery(id+"F10.opExtrude","SWEPT_FACE",FACE,{"disambiguationData":[OSD([subQ1])]});var subQ8=sQuery(id+"F0.wireOp",EDGE,"E4.2");var subQ22=makeQuery(id+"F14.boolean.opBoolean","SPLIT",EDGE,{"disambiguationData":[TD([subQ4])],"derivedFrom":makeQuery(id+"F10.boolean.opBoolean","SPLIT",EDGE,{"disambiguationData":[TD([subQ4])],"derivedFrom":makeQuery(id+"F1.opExtrude","CAP_EDGE",EDGE,{"disambiguationData":[OSD([subQ8])],"isStart":true})})});Q18=makeQuery(id+"F21.imprint","IMPRINT",FACE,{"disambiguationData":[TD([[makeQuery(id+"F21.imprint","IMPRINT",EDGE,{"derivedFrom":subQ22}),1.0]])]});}
            var Q19;
            {var subQ2=sQuery(id+"F9.wireOp",EDGE,"E17");var subQ4=sQuery(id+"F9.wireOp",EDGE,"E23");var subQ7=makeQuery(id+"F10.opExtrude","SWEPT_FACE",FACE,{"disambiguationData":[OSD([subQ4])]});var subQ10=sQuery(id+"F0.wireOp",EDGE,"E4.2");var subQ20=makeQuery(id+"F10.opExtrude","SWEPT_FACE",FACE,{"disambiguationData":[OSD([subQ2])]});var subQ24=makeQuery(id+"F14.boolean.opBoolean","SPLIT",EDGE,{"disambiguationData":[TD([subQ7])],"derivedFrom":makeQuery(id+"F10.boolean.opBoolean","SPLIT",EDGE,{"disambiguationData":[TD([subQ20])],"derivedFrom":makeQuery(id+"F1.opExtrude","CAP_EDGE",EDGE,{"disambiguationData":[OSD([subQ10])],"isStart":true})})});Q19=makeQuery(id+"F21.imprint","IMPRINT",FACE,{"disambiguationData":[TD([[makeQuery(id+"F21.imprint","IMPRINT",EDGE,{"derivedFrom":subQ24}),1.0]])]});}
            var Q20;
            {var subQ3=sQuery(id+"F9.wireOp",EDGE,"E21");var subQ6=sQuery(id+"F0.wireOp",EDGE,"E4.3");var subQ7=sQuery(id+"F0.wireOp",EDGE,"E4.2");var subQ11=makeQuery(id+"F10.opExtrude","SWEPT_FACE",FACE,{"disambiguationData":[OSD([subQ3])]});var subQ22=makeQuery(id+"F14.boolean.opBoolean","SPLIT",EDGE,{"disambiguationData":[TD([subQ11])],"derivedFrom":makeQuery(id+"F10.boolean.opBoolean","SPLIT",EDGE,{"disambiguationData":[TD([makeQuery(id+"F1.opExtrude","SWEPT_FACE",FACE,{"disambiguationData":[OSD([subQ6])]})])],"derivedFrom":makeQuery(id+"F1.opExtrude","CAP_EDGE",EDGE,{"disambiguationData":[OSD([subQ7])],"isStart":true})})});Q20=makeQuery(id+"F21.imprint","IMPRINT",FACE,{"disambiguationData":[TD([[makeQuery(id+"F21.imprint","IMPRINT",EDGE,{"derivedFrom":subQ22}),1.0]])]});}
            extrude(context, id + "F22", {"entities" : qUnion([Q0, Q1, Q2, Q3, Q4, Q5, Q6, Q7, Q8, Q9, Q10, Q11, Q12, Q13, Q14, Q15, Q16, Q17, Q18, Q19, Q20]), "depth" : 1.27 * mm});
        }
    });
